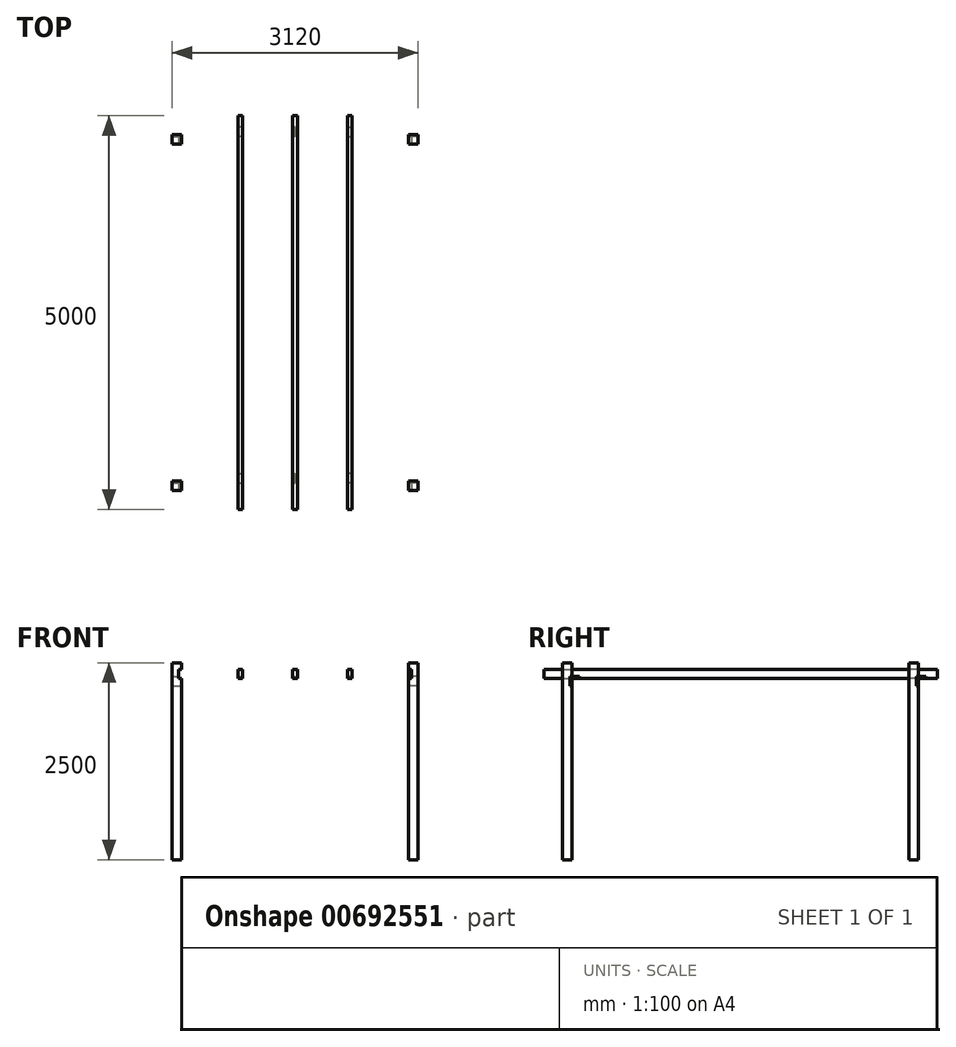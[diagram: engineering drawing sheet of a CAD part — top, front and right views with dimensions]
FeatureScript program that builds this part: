
annotation { "Feature Type Name" : "Feature", "Feature Type Description" : "" }
export const myFeature = defineFeature(function(context is Context, id is Id, definition is map)
    precondition{}
    {
        {
            var Q0;
            Q0=qCreatedBy(makeId("Top.planeOp"),FACE);
            var sketch = newSketch(context, id + "F0", { "sketchPlane" : qUnion([Q0])});
            skLineSegment(sketch, "E0.bottom", {"start": v(-1500, 2200) * mm, "end": v(1500, 2200) * mm, "construction": true});
            skLineSegment(sketch, "E0.top", {"start": v(-1500, -2200) * mm, "end": v(1500, -2200) * mm, "construction": true});
            skLineSegment(sketch, "E0.left", {"start": v(-1500, 2200) * mm, "end": v(-1500, -2200) * mm, "construction": true});
            skLineSegment(sketch, "E0.right", {"start": v(1500, 2200) * mm, "end": v(1500, -2200) * mm, "construction": true});
            skPoint(sketch, "E0.middle", {"position": v(0, 0) * mm});
            skSolve(sketch);
        }
        {
            var Q0;
            Q0=qCreatedBy(makeId("Top.planeOp"),FACE);
            var sketch = newSketch(context, id + "F1", { "sketchPlane" : qUnion([Q0])});
            skLineSegment(sketch, "E1.bottom", {"start": v(-1560, -2140) * mm, "end": v(-1440, -2140) * mm});
            skLineSegment(sketch, "E1.top", {"start": v(-1560, -2260) * mm, "end": v(-1440, -2260) * mm});
            skLineSegment(sketch, "E1.left", {"start": v(-1560, -2140) * mm, "end": v(-1560, -2260) * mm});
            skLineSegment(sketch, "E1.right", {"start": v(-1440, -2140) * mm, "end": v(-1440, -2260) * mm});
            skPoint(sketch, "E1.middle", {"position": v(-1500, -2200) * mm});
            skSolve(sketch);
        }
        {
            var Q0;
            Q0 = qSketchRegion(id + "F1", true);
            extrude(context, id + "F2", {"entities" : qUnion([Q0]), "depth" : 2500 * mm, "offsetDistance" : 25 * mm});
        }
        {
            var Q0;
            Q0=makeQuery(id+"F2.opExtrude","SWEPT_BODY",BODY,{"disambiguationData":[OSD([sQuery(id+"F1.wireOp",EDGE,"E1.bottom"),sQuery(id+"F1.wireOp",EDGE,"E1.top"),sQuery(id+"F1.wireOp",EDGE,"E1.left"),sQuery(id+"F1.wireOp",EDGE,"E1.right")])]});
            var Q1;
            Q1=qCreatedBy(makeId("Front.planeOp"),FACE);
            mirror(context, id + "F3", {"entities" : qUnion([Q0]), "mirrorPlane" : qUnion([Q1])});
        }
        {
            var Q0;
            Q0=makeQuery(id+"F2.opExtrude","SWEPT_BODY",BODY,{"disambiguationData":[OSD([sQuery(id+"F1.wireOp",EDGE,"E1.bottom"),sQuery(id+"F1.wireOp",EDGE,"E1.top"),sQuery(id+"F1.wireOp",EDGE,"E1.left"),sQuery(id+"F1.wireOp",EDGE,"E1.right")])]});
            var Q1;
            Q1=makeQuery(id+"F3.opPattern","COPY",BODY,{"derivedFrom":makeQuery(id+"F2.opExtrude","SWEPT_BODY",BODY,{"disambiguationData":[OSD([sQuery(id+"F1.wireOp",EDGE,"E1.bottom"),sQuery(id+"F1.wireOp",EDGE,"E1.top"),sQuery(id+"F1.wireOp",EDGE,"E1.left"),sQuery(id+"F1.wireOp",EDGE,"E1.right")])]}),"instanceName":"1"});
            var Q2;
            Q2=qCreatedBy(makeId("Right.planeOp"),FACE);
            mirror(context, id + "F4", {"entities" : qUnion([Q0, Q1]), "mirrorPlane" : qUnion([Q2])});
        }
        {
            var Q0;
            Q0=qCreatedBy(makeId("Front.planeOp"),FACE);
            var sketch = newSketch(context, id + "F5", { "sketchPlane" : qUnion([Q0])});
            skLineSegment(sketch, "E2", {"start": v(1560, 2300) * mm, "end": v(-1560, 2300) * mm, "construction": true});
            skLineSegment(sketch, "E3.bottom", {"start": v(-1480, 2420) * mm, "end": v(-1360, 2420) * mm});
            skLineSegment(sketch, "E3.top", {"start": v(-1480, 2300) * mm, "end": v(-1360, 2300) * mm});
            skLineSegment(sketch, "E3.left", {"start": v(-1480, 2420) * mm, "end": v(-1480, 2300) * mm});
            skLineSegment(sketch, "E3.right", {"start": v(-1360, 2420) * mm, "end": v(-1360, 2300) * mm});
            skPoint(sketch, "E3.middle", {"position": v(-1420, 2360) * mm});
            skSolve(sketch);
        }
        {
            var Q0;
            Q0 = qSketchRegion(id + "F5", true);
            var Q1;
            Q1=sQuery(id+"F0.wireOp",VERTEX,"E0.left.start");
            var Q2;
            Q2=sQuery(id+"F1.wireOp",VERTEX,"E1.middle");
            extrude(context, id + "F6", {"entities" : qUnion([Q0]), "endBound" : BoundingType.SYMMETRIC, "depth" : 5000 * mm, "endBoundEntityVertex" : qUnion([Q1]), "offsetDistance" : 25 * mm});
        }
        {
            var Q0;
            Q0 = qSketchRegion(id + "F5", true);
            extrude(context, id + "F7", {"entities" : qUnion([Q0]), "operationType" : NewBodyOperationType.REMOVE, "endBound" : BoundingType.SYMMETRIC, "oppositeDirection" : true, "depth" : 5000 * mm, "offsetDistance" : 25 * mm});
        }
        {
            var Q0;
            Q0=qCreatedBy(makeId("Front.planeOp"),FACE);
            var sketch = newSketch(context, id + "F8", { "sketchPlane" : qUnion([Q0])});
            skLineSegment(sketch, "E4", {"start": v(1560, 2420) * mm, "end": v(-1560, 2420) * mm, "construction": true});
            skLineSegment(sketch, "E5", {"start": v(0, 2420) * mm, "end": v(0, 0) * mm, "construction": true});
            skLineSegment(sketch, "E6.bottom", {"start": v(30, 2420) * mm, "end": v(-30, 2420) * mm});
            skLineSegment(sketch, "E6.top", {"start": v(30, 2300) * mm, "end": v(-30, 2300) * mm});
            skLineSegment(sketch, "E6.left", {"start": v(30, 2420) * mm, "end": v(30, 2300) * mm});
            skLineSegment(sketch, "E6.right", {"start": v(-30, 2420) * mm, "end": v(-30, 2300) * mm});
            skPoint(sketch, "E6.middle", {"position": v(0, 2360) * mm});
            skLineSegment(sketch, "E7", {"start": v(-30, 2360) * mm, "end": v(-1360, 2360) * mm, "construction": true});
            skLineSegment(sketch, "E8.bottom", {"start": v(-665, 2420) * mm, "end": v(-725, 2420) * mm});
            skLineSegment(sketch, "E8.top", {"start": v(-665, 2300) * mm, "end": v(-725, 2300) * mm});
            skLineSegment(sketch, "E8.left", {"start": v(-665, 2420) * mm, "end": v(-665, 2300) * mm});
            skLineSegment(sketch, "E8.right", {"start": v(-725, 2420) * mm, "end": v(-725, 2300) * mm});
            skPoint(sketch, "E8.middle", {"position": v(-695, 2360) * mm});
            skSolve(sketch);
        }
        {
            var Q0;
            Q0 = qSketchRegion(id + "F8", true);
            extrude(context, id + "F9", {"entities" : qUnion([Q0]), "endBound" : BoundingType.SYMMETRIC, "depth" : 5000 * mm, "offsetDistance" : 25 * mm});
        }
        {
            var Q0;
            Q0=qCreatedBy(makeId("Right.planeOp"),FACE);
            var sketch = newSketch(context, id + "F10", { "sketchPlane" : qUnion([Q0])});
            skLineSegment(sketch, "E9.bottom", {"start": v(2235, 2325) * mm, "end": v(2355, 2325) * mm});
            skLineSegment(sketch, "E9.top", {"start": v(2235, 2205) * mm, "end": v(2355, 2205) * mm});
            skLineSegment(sketch, "E9.left", {"start": v(2235, 2325) * mm, "end": v(2235, 2205) * mm});
            skLineSegment(sketch, "E9.right", {"start": v(2355, 2325) * mm, "end": v(2355, 2205) * mm});
            skPoint(sketch, "E9.middle", {"position": v(2295, 2265) * mm});
            skLineSegment(sketch, "E10", {"start": v(2235, 2205) * mm, "end": v(-2045, 2205) * mm, "construction": true});
            skLineSegment(sketch, "E11", {"start": v(2355, 2265) * mm, "end": v(2140, 2265) * mm, "construction": true});
            skLineSegment(sketch, "E12.bottom", {"start": v(-2045, 2205) * mm, "end": v(-2165, 2205) * mm});
            skLineSegment(sketch, "E12.top", {"start": v(-2045, 2325) * mm, "end": v(-2165, 2325) * mm});
            skLineSegment(sketch, "E12.left", {"start": v(-2045, 2205) * mm, "end": v(-2045, 2325) * mm});
            skLineSegment(sketch, "E12.right", {"start": v(-2165, 2205) * mm, "end": v(-2165, 2325) * mm});
            skSolve(sketch);
        }
        {
            var Q0;
            Q0 = qSketchRegion(id + "F10", true);
            extrude(context, id + "F11", {"entities" : qUnion([Q0]), "oppositeDirection" : true, "depth" : 1800 * mm, "offsetDistance" : 25 * mm});
        }
        {
            var Q0;
            Q0 = qSketchRegion(id + "F10", true);
            extrude(context, id + "F12", {"entities" : qUnion([Q0]), "operationType" : NewBodyOperationType.REMOVE, "endBound" : BoundingType.THROUGH_ALL, "oppositeDirection" : true, "depth" : 25 * mm, "offsetDistance" : 25 * mm});
        }
        {
            var Q0;
            Q0=makeQuery(id+"F9.opExtrude","SWEPT_BODY",BODY,{"disambiguationData":[OSD([sQuery(id+"F8.wireOp",EDGE,"E8.bottom"),sQuery(id+"F8.wireOp",EDGE,"E8.top"),sQuery(id+"F8.wireOp",EDGE,"E8.left"),sQuery(id+"F8.wireOp",EDGE,"E8.right")])]});
            var Q1;
            Q1=makeQuery(id+"F6.opExtrude","SWEPT_BODY",BODY,{"disambiguationData":[OSD([sQuery(id+"F5.wireOp",EDGE,"E3.bottom"),sQuery(id+"F5.wireOp",EDGE,"E3.top"),sQuery(id+"F5.wireOp",EDGE,"E3.left"),sQuery(id+"F5.wireOp",EDGE,"E3.right")])]});
            var Q2;
            Q2=makeQuery(id+"F11.opExtrude","SWEPT_BODY",BODY,{"disambiguationData":[OSD([sQuery(id+"F10.wireOp",EDGE,"E9.bottom"),sQuery(id+"F10.wireOp",EDGE,"E9.top"),sQuery(id+"F10.wireOp",EDGE,"E9.left"),sQuery(id+"F10.wireOp",EDGE,"E9.right")])]});
            var Q3;
            Q3=makeQuery(id+"F11.opExtrude","SWEPT_BODY",BODY,{"disambiguationData":[OSD([sQuery(id+"F10.wireOp",EDGE,"v6hjvFlb-WhWx-oe9K-3YFU-TFhj817QYztr.bottom"),sQuery(id+"F10.wireOp",EDGE,"v6hjvFlb-WhWx-oe9K-3YFU-TFhj817QYztr.top"),sQuery(id+"F10.wireOp",EDGE,"v6hjvFlb-WhWx-oe9K-3YFU-TFhj817QYztr.left"),sQuery(id+"F10.wireOp",EDGE,"v6hjvFlb-WhWx-oe9K-3YFU-TFhj817QYztr.right")])]});
            var Q4;
            Q4=makeQuery(id+"F2.opExtrude","SWEPT_BODY",BODY,{"disambiguationData":[OSD([sQuery(id+"F1.wireOp",EDGE,"E1.bottom"),sQuery(id+"F1.wireOp",EDGE,"E1.top"),sQuery(id+"F1.wireOp",EDGE,"E1.left"),sQuery(id+"F1.wireOp",EDGE,"E1.right")])]});
            var Q5;
            Q5=makeQuery(id+"F3.opPattern","COPY",BODY,{"derivedFrom":makeQuery(id+"F2.opExtrude","SWEPT_BODY",BODY,{"disambiguationData":[OSD([sQuery(id+"F1.wireOp",EDGE,"E1.bottom"),sQuery(id+"F1.wireOp",EDGE,"E1.top"),sQuery(id+"F1.wireOp",EDGE,"E1.left"),sQuery(id+"F1.wireOp",EDGE,"E1.right")])]}),"instanceName":"1"});
            var Q6;
            Q6=makeQuery(id+"F11.opExtrude","SWEPT_BODY",BODY,{"disambiguationData":[OSD([sQuery(id+"F10.wireOp",EDGE,"E12.bottom"),sQuery(id+"F10.wireOp",EDGE,"E12.top"),sQuery(id+"F10.wireOp",EDGE,"E12.left"),sQuery(id+"F10.wireOp",EDGE,"E12.right")])]});
            var Q7;
            Q7=qCreatedBy(makeId("Right.planeOp"),FACE);
            mirror(context, id + "F13", {"entities" : qUnion([Q0, Q1, Q2, Q3, Q4, Q5, Q6]), "mirrorPlane" : qUnion([Q7])});
        }
        {
            var Q0;
            Q0=qCreatedBy(makeId("Front.planeOp"),FACE);
            var sketch = newSketch(context, id + "F14", { "sketchPlane" : qUnion([Q0])});
            skCircle(sketch, "E13", {"center": v(1800, 2160) * mm, "radius": 125 * mm});
            skPoint(sketch, "E14", {"position": v(1800, 2285) * mm});
            skLineSegment(sketch, "E15", {"start": v(1800, 2160) * mm, "end": v(-1800, 2160) * mm, "construction": true});
            skLineSegment(sketch, "E16", {"start": v(0, 2160) * mm, "end": v(0, 2205) * mm, "construction": true});
            skCircle(sketch, "E17", {"center": v(-1800, 2160) * mm, "radius": 125 * mm});
            skSolve(sketch);
        }
        {
            var Q0;
            Q0 = qSketchRegion(id + "F14", true);
            extrude(context, id + "F15", {"entities" : qUnion([Q0]), "operationType" : NewBodyOperationType.REMOVE, "endBound" : BoundingType.THROUGH_ALL, "depth" : 25 * mm, "offsetDistance" : 25 * mm, "hasSecondDirection" : true, "secondDirectionBound" : SecondDirectionBoundingType.THROUGH_ALL, "secondDirectionOppositeDirection" : true, "secondDirectionDepth" : 25 * mm});
        }
    });
